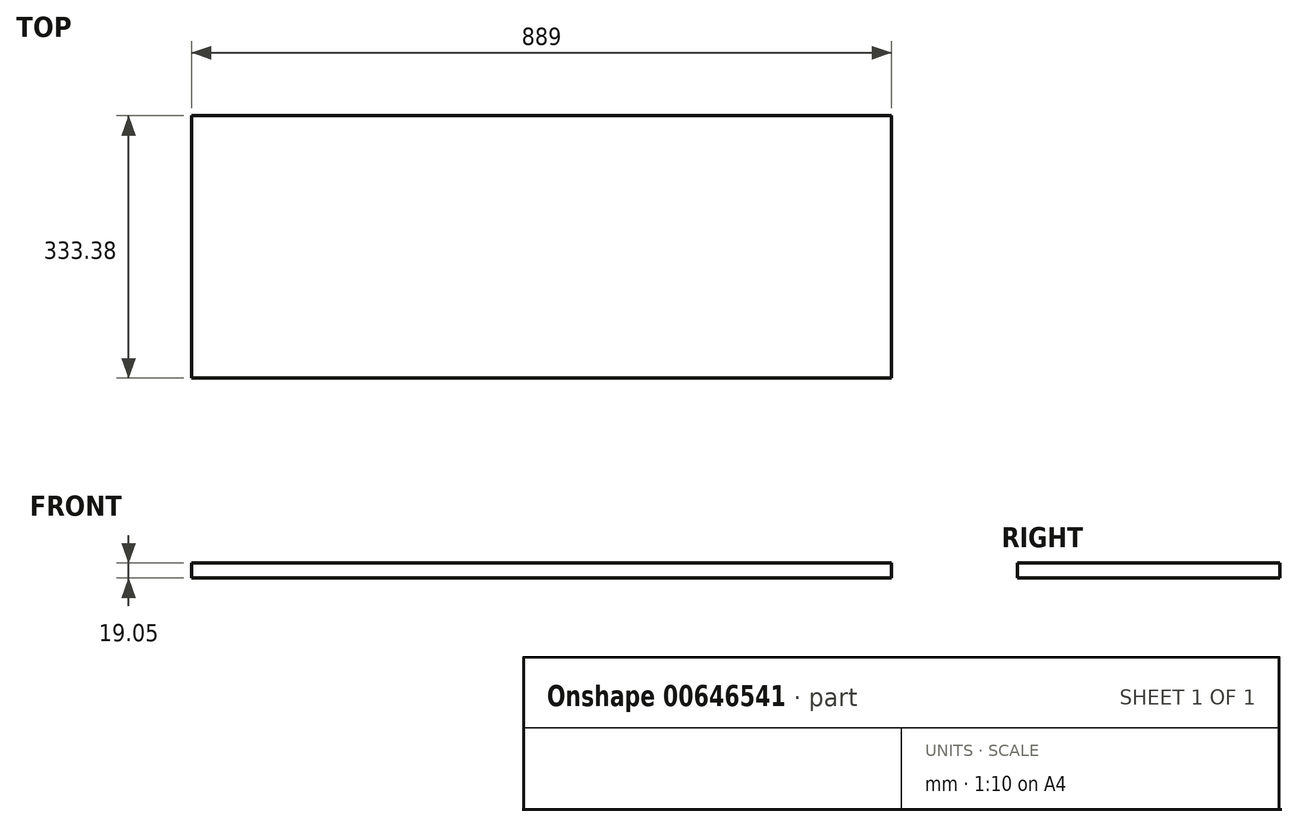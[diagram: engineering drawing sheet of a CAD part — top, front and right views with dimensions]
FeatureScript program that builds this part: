
annotation { "Feature Type Name" : "Feature", "Feature Type Description" : "" }
export const myFeature = defineFeature(function(context is Context, id is Id, definition is map)
    precondition{}
    {
        {
            var Q0;
            Q0=qCreatedBy(makeId("Top.planeOp"),FACE);
            var sketch = newSketch(context, id + "F0", { "sketchPlane" : qUnion([Q0])});
            skLineSegment(sketch, "E0.bottom", {"start": v(-444.5, 166.69) * mm, "end": v(444.5, 166.69) * mm});
            skLineSegment(sketch, "E0.top", {"start": v(-444.5, -166.69) * mm, "end": v(444.5, -166.69) * mm});
            skLineSegment(sketch, "E0.left", {"start": v(-444.5, 166.69) * mm, "end": v(-444.5, -166.69) * mm});
            skLineSegment(sketch, "E0.right", {"start": v(444.5, 166.69) * mm, "end": v(444.5, -166.69) * mm});
            skPoint(sketch, "E0.middle", {"position": v(0, 0) * mm});
            skSolve(sketch);
        }
        {
            var Q0;
            Q0=makeQuery(id+"F0.imprint","IMPRINT",FACE,{"disambiguationData":[TD([[makeQuery(id+"F0.imprint","IMPRINT",EDGE,{"derivedFrom":sQuery(id+"F0.wireOp",EDGE,"E0.bottom")}),-1.0]])]});
            extrude(context, id + "F1", {"entities" : qUnion([Q0]), "depth" : 19.05 * mm, "offsetDistance" : 25.4 * mm});
        }
    });
